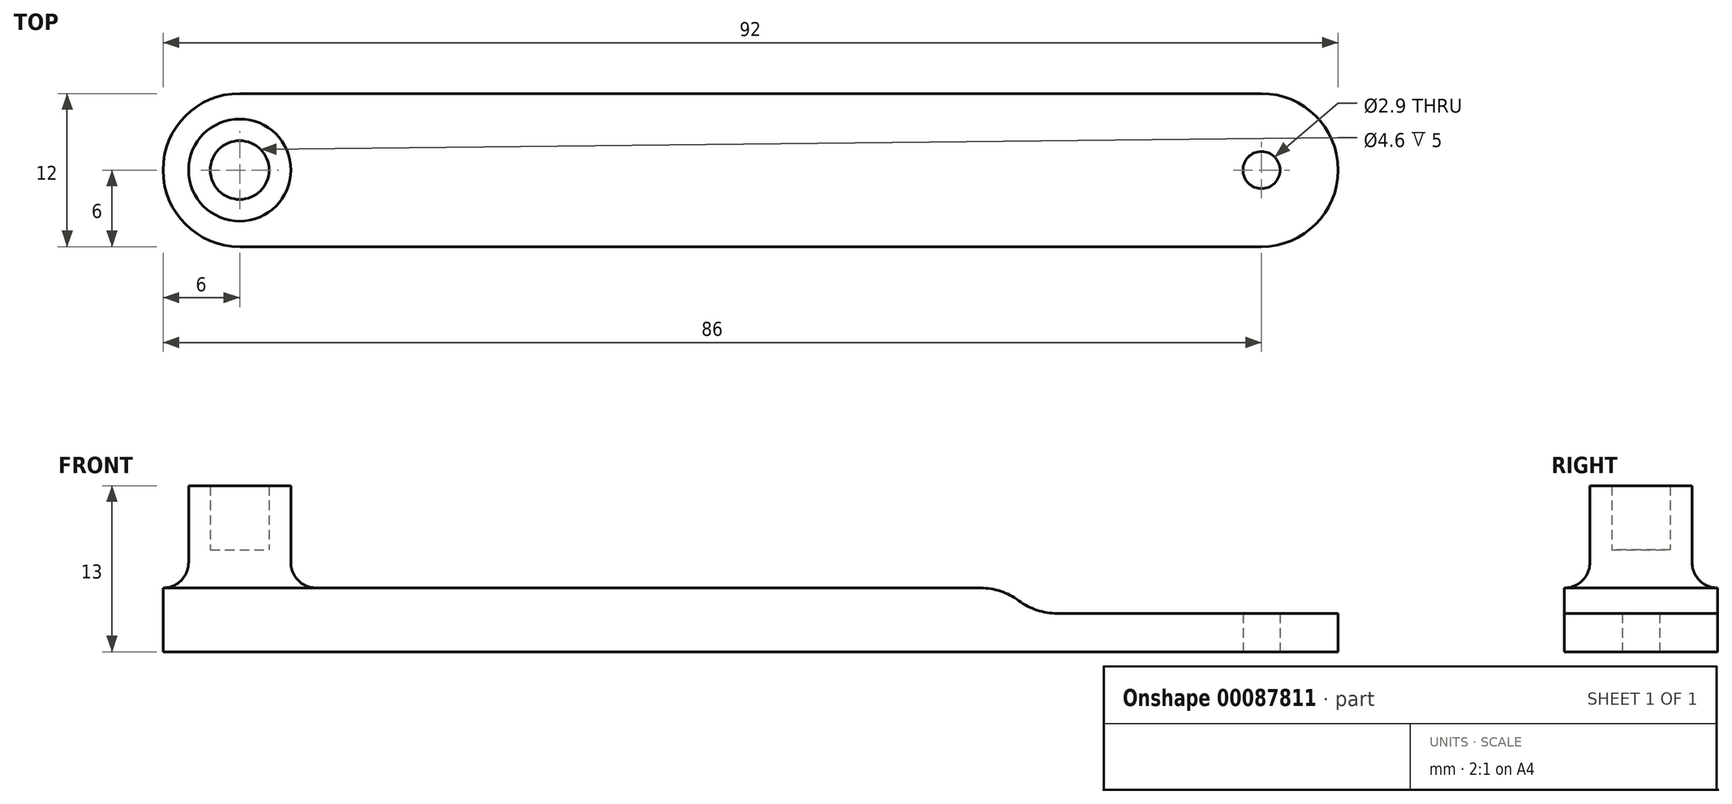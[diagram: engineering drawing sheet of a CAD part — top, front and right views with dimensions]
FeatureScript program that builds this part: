
annotation { "Feature Type Name" : "Feature", "Feature Type Description" : "" }
export const myFeature = defineFeature(function(context is Context, id is Id, definition is map)
    precondition{}
    {
        {
            var Q0;
            Q0=qCreatedBy(makeId("Top.planeOp"),FACE);
            var sketch = newSketch(context, id + "F0", { "sketchPlane" : qUnion([Q0])});
            skArc(sketch, "E0", {"start": v(0, -6) * mm, "mid": v(6, 0) * mm, "end": v(0, 6) * mm});
            skLineSegment(sketch, "E1", {"start": v(0, 6) * mm, "end": v(-80, 6) * mm});
            skLineSegment(sketch, "E2", {"start": v(0, -6) * mm, "end": v(-80, -6) * mm});
            skArc(sketch, "E3", {"start": v(-80, 6) * mm, "mid": v(-86, 0) * mm, "end": v(-80, -6) * mm});
            skPoint(sketch, "E3.second.point", {"position": v(-80, 6) * mm});
            skCircle(sketch, "E4", {"center": v(-80, 0) * mm, "radius": 3.75 * mm});
            skCircle(sketch, "E5", {"center": v(0, 0) * mm, "radius": 1.45 * mm});
            skSolve(sketch);
        }
        {
            var Q0;
            Q0=qSketchRegion(id+"F0",true);
            extrude(context, id + "F1", {"entities" : qUnion([Q0]), "depth" : 5 * mm});
        }
        {
            var Q0;
            Q0=makeQuery(id+"F1.opExtrude","CAP_FACE",FACE,{"disambiguationData":[OSD([sQuery(id+"F0.wireOp",EDGE,"E0"),sQuery(id+"F0.wireOp",EDGE,"E1"),sQuery(id+"F0.wireOp",EDGE,"E2"),sQuery(id+"F0.wireOp",EDGE,"E3"),sQuery(id+"F0.wireOp",EDGE,"E4"),sQuery(id+"F0.wireOp",EDGE,"E5")])],"isStart":true});
            var sketch = newSketch(context, id + "F2", { "sketchPlane" : qUnion([Q0])});
            skCircle(sketch, "E6", {"center": v(-80, 0) * mm, "radius": 4 * mm});
            skCircle(sketch, "E7", {"center": v(-80, 0) * mm, "radius": 2.3 * mm});
            skSolve(sketch);
        }
        {
            var Q0;
            Q0 = qSketchRegion(id + "F2", true);
            extrude(context, id + "F3", {"entities" : qUnion([Q0]), "operationType" : NewBodyOperationType.ADD, "oppositeDirection" : true, "depth" : 13 * mm});
        }
        {
            var Q0;
            Q0=makeQuery(id+"F2.imprint","IMPRINT",FACE,{"disambiguationData":[TD([[makeQuery(id+"F2.imprint","IMPRINT",EDGE,{"derivedFrom":sQuery(id+"F2.wireOp",EDGE,"E7")}),1.0]])]});
            extrude(context, id + "F4", {"entities" : qUnion([Q0]), "operationType" : NewBodyOperationType.ADD, "oppositeDirection" : true, "depth" : 8 * mm});
        }
        {
            var Q0;
            Q0=makeQuery(id+"F3.boolean.opBoolean","INTERSECT",EDGE,{"derivedFrom":[makeQuery(id+"F1.opExtrude","CAP_FACE",FACE,{"disambiguationData":[OSD([sQuery(id+"F0.wireOp",EDGE,"E0"),sQuery(id+"F0.wireOp",EDGE,"E1"),sQuery(id+"F0.wireOp",EDGE,"E2"),sQuery(id+"F0.wireOp",EDGE,"E3"),sQuery(id+"F0.wireOp",EDGE,"E4"),sQuery(id+"F0.wireOp",EDGE,"E5")])],"isStart":false}),makeQuery(id+"F3.opExtrude","SWEPT_FACE",FACE,{"disambiguationData":[OSD([sQuery(id+"F2.wireOp",EDGE,"E6")])]})]});
            fillet(context, id + "F5", {"entities" : qUnion([Q0]), "radius" : 2 * mm, "tangentPropagation" : true, "allowEdgeOverflow" : false});
        }
        {
            var Q0;
            Q0=makeQuery(id+"F1.opExtrude","CAP_FACE",FACE,{"disambiguationData":[OSD([sQuery(id+"F0.wireOp",EDGE,"E0"),sQuery(id+"F0.wireOp",EDGE,"E1"),sQuery(id+"F0.wireOp",EDGE,"E2"),sQuery(id+"F0.wireOp",EDGE,"E3"),sQuery(id+"F0.wireOp",EDGE,"E4"),sQuery(id+"F0.wireOp",EDGE,"E5")])],"isStart":false});
            var sketch = newSketch(context, id + "F6", { "sketchPlane" : qUnion([Q0])});
            skLineSegment(sketch, "E8.bottom", {"start": v(-20, 6.5) * mm, "end": v(6, 6.5) * mm});
            skLineSegment(sketch, "E8.top", {"start": v(-20, -6.5) * mm, "end": v(6, -6.5) * mm});
            skLineSegment(sketch, "E8.left", {"start": v(-20, 6.5) * mm, "end": v(-20, -6.5) * mm});
            skLineSegment(sketch, "E8.right", {"start": v(6, 6.5) * mm, "end": v(6, -6.5) * mm});
            skPoint(sketch, "E9", {"position": v(-20, 0) * mm});
            skSolve(sketch);
        }
        {
            var Q0;
            Q0 = qSketchRegion(id + "F6", true);
            extrude(context, id + "F7", {"entities" : qUnion([Q0]), "operationType" : NewBodyOperationType.REMOVE, "oppositeDirection" : true, "depth" : 2 * mm});
        }
        {
            var Q0;
            Q0=makeQuery(id+"F7.boolean.opBoolean","COPY",EDGE,{"derivedFrom":makeQuery(id+"F7.opExtrude","CAP_EDGE",EDGE,{"disambiguationData":[OSD([sQuery(id+"F6.wireOp",EDGE,"E8.left")])],"isStart":false})});
            fillet(context, id + "F8", {"entities" : qUnion([Q0]), "radius" : 5 * mm, "tangentPropagation" : true, "allowEdgeOverflow" : false});
        }
        {
            var Q0;
            Q0=makeQuery(id+"F8.opFillet","BLEND_EDGE",EDGE,{"blendedFrom":[makeQuery(id+"F7.boolean.opBoolean","COPY",EDGE,{"derivedFrom":makeQuery(id+"F7.opExtrude","CAP_EDGE",EDGE,{"disambiguationData":[OSD([sQuery(id+"F6.wireOp",EDGE,"E8.left")])],"isStart":false})}),makeQuery(id+"F1.opExtrude","CAP_FACE",FACE,{"disambiguationData":[OSD([sQuery(id+"F0.wireOp",EDGE,"E0"),sQuery(id+"F0.wireOp",EDGE,"E1"),sQuery(id+"F0.wireOp",EDGE,"E2"),sQuery(id+"F0.wireOp",EDGE,"E3"),sQuery(id+"F0.wireOp",EDGE,"E4"),sQuery(id+"F0.wireOp",EDGE,"E5")])],"isStart":false})],"blendedInto":[makeQuery(id+"F1.opExtrude","CAP_FACE",FACE,{"disambiguationData":[OSD([sQuery(id+"F0.wireOp",EDGE,"E0"),sQuery(id+"F0.wireOp",EDGE,"E1"),sQuery(id+"F0.wireOp",EDGE,"E2"),sQuery(id+"F0.wireOp",EDGE,"E3"),sQuery(id+"F0.wireOp",EDGE,"E4"),sQuery(id+"F0.wireOp",EDGE,"E5")])],"isStart":false})]});
            fillet(context, id + "F9", {"entities" : qUnion([Q0]), "radius" : 5 * mm, "tangentPropagation" : true, "allowEdgeOverflow" : false});
        }
    });
